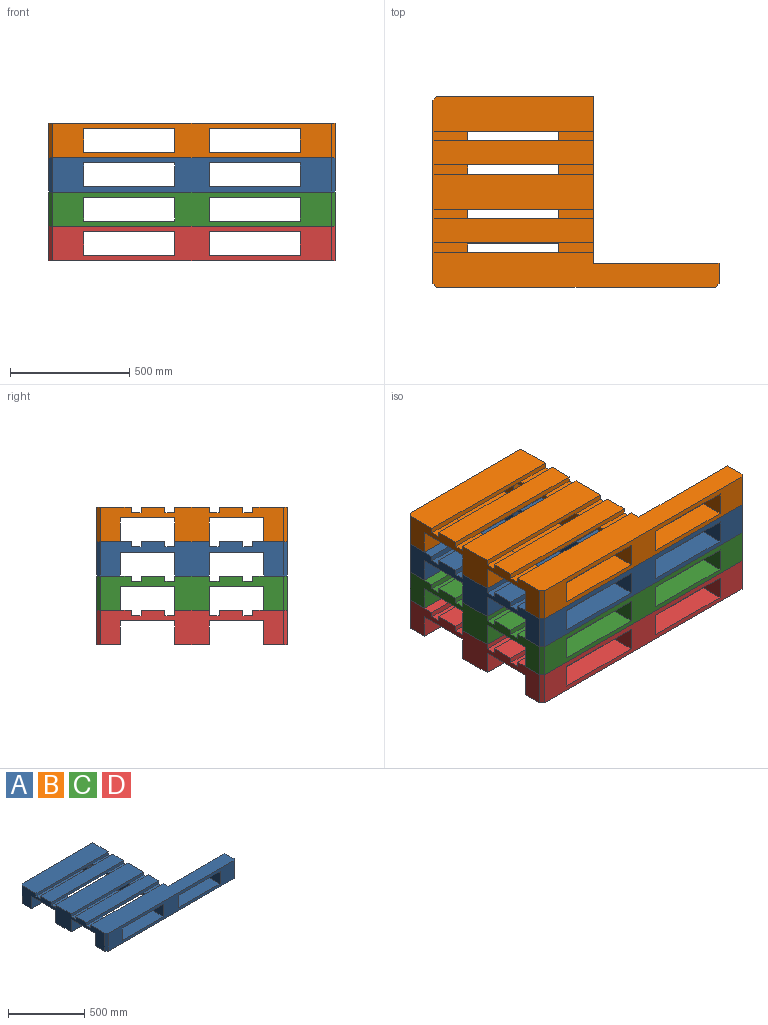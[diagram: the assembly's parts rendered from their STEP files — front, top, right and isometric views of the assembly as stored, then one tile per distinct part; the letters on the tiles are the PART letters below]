
ASSEMBLY  parts=4 mates=9
PART A: 53 faces, bbox 1200x800x144 mm
  f0: plane 1170x144mm, normal (0,-1,0), area 91980mm2, adj f1,f10,f11,f12,f19,f28,f30,f43
  f1: plane 100x100mm, normal (-1,0,0), area 10000mm2, adj f0,f12,f42,f43
  f2: plane 657.5x144mm, normal (0,1,0), area 56430mm2, adj f10,f11,f19,f21,f23,f40,f41,f50
  f3: plane 144x85mm, normal (1,0,0), area 12240mm2, adj f30,f42,f44,f51
  f4: plane 227.5x145mm, normal (0,0,-1), area 32987.5mm2, adj f10,f11,f39,f46
  f5: plane 227.5x145mm, normal (0,0,-1), area 32987.5mm2, adj f10,f11,f42,f47
  f6: plane 145x41.25mm, normal (0,0,1), area 5981.3mm2, adj f10,f11,f22,f25
  f7: plane 145x41.25mm, normal (0,0,1), area 5981.3mm2, adj f10,f11,f26,f37
  f8: plane 145x41.25mm, normal (0,0,1), area 5981.2mm2, adj f10,f11,f29,f32
  f9: plane 145x41.25mm, normal (0,0,1), area 5981.2mm2, adj f10,f11,f33,f36
  f10: plane 800x144mm, normal (1,0,0), area 61670mm2, adj f0,f2,f4,f5,f6,f7,f8,f9
  f11: plane 800x100mm, normal (-1,0,0), area 44510mm2, adj f0,f2,f4,f5,f6,f7,f8,f9
  f12: plane 382.5x100mm, normal (0,0,-1), area 38250mm2, adj f0,f1,f10,f42
  f13: plane 227.5x145mm, normal (0,0,-1), area 32987.5mm2, adj f19,f20,f42,f47
  f14: plane 227.5x145mm, normal (0,0,-1), area 32987.5mm2, adj f19,f20,f39,f46
  f15: plane 145x41.25mm, normal (0,0,1), area 5981.2mm2, adj f19,f20,f26,f37
  f16: plane 145x41.25mm, normal (0,0,1), area 5981.2mm2, adj f19,f20,f33,f36
  f17: plane 145x41.25mm, normal (0,0,1), area 5981.2mm2, adj f19,f20,f29,f32
  f18: plane 145x41.25mm, normal (0,0,1), area 5981.2mm2, adj f19,f20,f22,f25
  f19: plane 800x100mm, normal (1,0,0), area 44510mm2, adj f0,f2,f13,f14,f15,f16,f17,f18
  f20: plane 770x144mm, normal (-1,0,0), area 61750mm2, adj f13,f14,f15,f16,f17,f18,f22,f23
  f21: plane 382.5x145mm, normal (0,0,-1), area 55462.5mm2, adj f2,f11,f19,f22
  f22: plane 672.5x22mm, normal (0,-1,0), area 14795mm2, adj f6,f10,f18,f20,f21,f23
  f23: plane 672.5x145mm, normal (0,0,1), area 97400mm2, adj f2,f10,f20,f22,f50
  f24: plane 382.5x100mm, normal (0,0,-1), area 38250mm2, adj f11,f19,f25,f26
  f25: plane 672.5x22mm, normal (0,1,0), area 14795mm2, adj f6,f10,f18,f20,f24,f27
  f26: plane 672.5x22mm, normal (0,-1,0), area 14795mm2, adj f7,f10,f15,f20,f24,f27
  f27: plane 672.5x100mm, normal (0,0,1), area 67250mm2, adj f10,f20,f25,f26
  f28: plane 382.5x145mm, normal (0,0,-1), area 55462.5mm2, adj f0,f11,f19,f29
  f29: plane 672.5x22mm, normal (0,1,0), area 14795mm2, adj f8,f10,f17,f20,f28,f30
  f30: plane 1200x145mm, normal (0,0,1), area 150037.5mm2, adj f0,f3,f10,f20,f29,f42,f51,f52
  f31: plane 382.5x100mm, normal (0,0,-1), area 38250mm2, adj f11,f19,f32,f33
  f32: plane 672.5x22mm, normal (0,-1,0), area 14795mm2, adj f8,f10,f17,f20,f31,f34
  f33: plane 672.5x22mm, normal (0,1,0), area 14795mm2, adj f9,f10,f16,f20,f31,f34
  f34: plane 672.5x100mm, normal (0,0,1), area 67250mm2, adj f10,f20,f32,f33
  f35: plane 382.5x145mm, normal (0,0,-1), area 55462.5mm2, adj f11,f19,f36,f37
  f36: plane 672.5x22mm, normal (0,-1,0), area 14795mm2, adj f9,f10,f16,f20,f35,f38
  f37: plane 672.5x22mm, normal (0,1,0), area 14795mm2, adj f7,f10,f15,f20,f35,f38
  f38: plane 672.5x145mm, normal (0,0,1), area 97512.5mm2, adj f10,f20,f36,f37
  f39: plane 672.5x100mm, normal (0,-1,0), area 37415mm2, adj f4,f10,f11,f14,f19,f20,f40,f41
  f40: plane 672.5x100mm, normal (0,0,-1), area 67137.5mm2, adj f2,f10,f20,f39,f50
  f41: plane 382.5x100mm, normal (0,0,1), area 38250mm2, adj f2,f11,f19,f39
  f42: plane 1200x144mm, normal (0,1,0), area 75125mm2, adj f1,f3,f5,f10,f11,f12,f13,f19
  f43: plane 382.5x100mm, normal (0,0,1), area 38250mm2, adj f0,f1,f10,f42
  f44: plane 1200x100mm, normal (0,0,-1), area 119775mm2, adj f0,f3,f20,f42,f51,f52
  f45: plane 382.5x100mm, normal (0,0,1), area 38250mm2, adj f0,f11,f19,f42
  f46: plane 672.5x100mm, normal (0,1,0), area 37415mm2, adj f4,f10,f11,f14,f19,f20,f48,f49
  f47: plane 672.5x100mm, normal (0,-1,0), area 37415mm2, adj f5,f10,f11,f13,f19,f20,f48,f49
  f48: plane 672.5x145mm, normal (0,0,-1), area 97512.5mm2, adj f10,f20,f46,f47
  f49: plane 382.5x145mm, normal (0,0,1), area 55462.5mm2, adj f11,f19,f46,f47
  f50: plane 144x15mm, normal (-0.71,0.71,0), area 3054.7mm2, adj f2,f20,f23,f40
  f51: plane 144x15mm, normal (0.71,-0.71,0), area 3054.7mm2, adj f0,f3,f30,f44
  f52: plane 144x15mm, normal (-0.71,-0.71,0), area 3054.7mm2, adj f0,f20,f30,f44
PART B: same geometry as A
PART C: same geometry as A
PART D: same geometry as A
PLACE A t=(0,0,288)mm
PLACE B t=(0,0,432)mm
PLACE C t=(0,0,144)mm
PLACE D at identity fixed
MATE planar A.f48 <-> C.f38  axis (0,0,-1) through (-263.75,0,144)mm
MATE planar C.f0 <-> D.f0  axis (0,-1,0) through (455,-400,72)mm
MATE planar C.f3 <-> D.f3  axis (1,0,0) through (600,-342.5,72)mm
MATE planar B.f0 <-> A.f0  axis (0,-1,0) through (0,-400,360)mm
MATE planar B.f48 <-> A.f38  axis (0,0,-1) through (-263.75,0,288)mm
MATE planar D.f3 <-> A.f3  axis (1,0,0) through (600,-342.5,-72)mm
MATE planar B.f3 <-> A.f3  axis (1,0,0) through (600,-342.5,360)mm
MATE planar D.f38 <-> C.f48  axis (0,0,1) through (-263.75,0,0)mm
MATE planar C.f0 <-> A.f0  axis (0,-1,0) through (0,-400,72)mm
